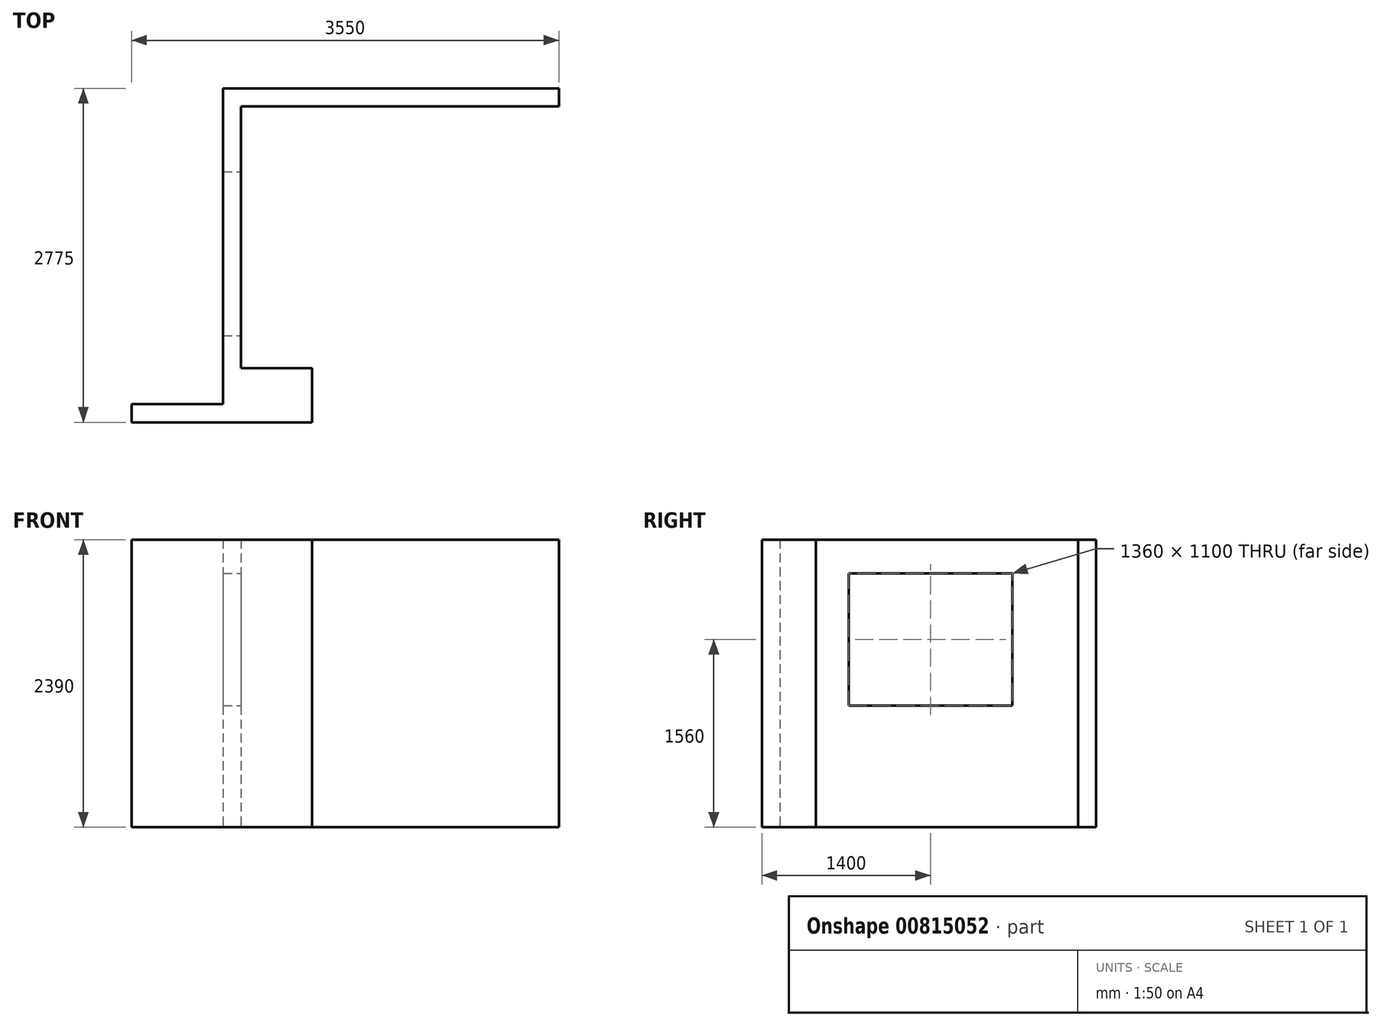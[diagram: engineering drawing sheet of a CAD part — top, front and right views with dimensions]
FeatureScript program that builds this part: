
annotation { "Feature Type Name" : "Feature", "Feature Type Description" : "" }
export const myFeature = defineFeature(function(context is Context, id is Id, definition is map)
    precondition{}
    {
        {
            var Q0;
            Q0=qCreatedBy(makeId("Top.planeOp"),FACE);
            var sketch = newSketch(context, id + "F0", { "sketchPlane" : qUnion([Q0])});
            skLineSegment(sketch, "E0", {"start": v(566.4, 2097.08) * mm, "end": v(566.4, -527.92) * mm});
            skLineSegment(sketch, "E1", {"start": v(566.4, -527.92) * mm, "end": v(716.4, -527.92) * mm});
            skLineSegment(sketch, "E2", {"start": v(716.4, -527.92) * mm, "end": v(716.4, 2247.08) * mm});
            skLineSegment(sketch, "E3", {"start": v(566.4, 2097.08) * mm, "end": v(-2083.6, 2097.08) * mm});
            skLineSegment(sketch, "E4", {"start": v(-2083.6, 2097.08) * mm, "end": v(-2083.6, -77.92) * mm});
            skLineSegment(sketch, "E5", {"start": v(-2083.6, -77.92) * mm, "end": v(-1493.6, -77.92) * mm});
            skLineSegment(sketch, "E6", {"start": v(716.4, 2247.08) * mm, "end": v(-2233.6, 2247.08) * mm});
            skLineSegment(sketch, "E7", {"start": v(-2233.6, 2247.08) * mm, "end": v(-2233.6, -377.92) * mm});
            skLineSegment(sketch, "E8", {"start": v(-2993.6, -527.92) * mm, "end": v(-2993.6, -377.92) * mm});
            skLineSegment(sketch, "E9", {"start": v(-2993.6, -377.92) * mm, "end": v(-2233.6, -377.92) * mm});
            skLineSegment(sketch, "E10", {"start": v(-1493.6, -527.92) * mm, "end": v(-2993.6, -527.92) * mm});
            skLineSegment(sketch, "E11", {"start": v(1616.4, -292.92) * mm, "end": v(2408.2, -292.92) * mm});
            skLineSegment(sketch, "E12", {"start": v(1616.4, 97.08) * mm, "end": v(1616.4, 97.08) * mm});
            skLineSegment(sketch, "E13", {"start": v(1616.4, 1097.08) * mm, "end": v(1616.4, 2097.08) * mm});
            skLineSegment(sketch, "E14", {"start": v(1616.4, 1097.08) * mm, "end": v(1616.4, 1097.08) * mm});
            skLineSegment(sketch, "E15", {"start": v(1616.4, 97.08) * mm, "end": v(2408.2, 97.08) * mm});
            skLineSegment(sketch, "E16", {"start": v(1616.4, -292.92) * mm, "end": v(1616.4, 97.08) * mm});
            skLineSegment(sketch, "E17", {"start": v(1616.4, 1097.08) * mm, "end": v(2417.61, 1097.08) * mm});
            skLineSegment(sketch, "E18", {"start": v(2408.2, -292.92) * mm, "end": v(2408.2, -7632.92) * mm});
            skLineSegment(sketch, "E19", {"start": v(2408.2, -7632.92) * mm, "end": v(-2131.8, -7632.92) * mm});
            skLineSegment(sketch, "E20", {"start": v(-2131.8, -7632.92) * mm, "end": v(-2131.8, -5762.92) * mm});
            skLineSegment(sketch, "E21", {"start": v(-2131.8, -5762.92) * mm, "end": v(-1531.8, -5762.92) * mm});
            skLineSegment(sketch, "E22", {"start": v(-1531.8, -5762.92) * mm, "end": v(-1531.8, -5407.77) * mm});
            skLineSegment(sketch, "E23", {"start": v(-1531.8, -5407.77) * mm, "end": v(-3031.8, -5407.77) * mm});
            skLineSegment(sketch, "E24", {"start": v(-3031.8, -5407.77) * mm, "end": v(-3031.8, -5557.77) * mm});
            skLineSegment(sketch, "E25", {"start": v(2408.2, 97.08) * mm, "end": v(2558.2, 97.08) * mm});
            skLineSegment(sketch, "E26", {"start": v(2558.2, 97.08) * mm, "end": v(2558.2, -7787.07) * mm});
            skLineSegment(sketch, "E27.0", {"start": v(2558.2, -7782.92) * mm, "end": v(-2281.8, -7782.92) * mm});
            skLineSegment(sketch, "E28.0", {"start": v(-2281.8, -7782.92) * mm, "end": v(-2281.8, -5557.77) * mm});
            skLineSegment(sketch, "E29.0", {"start": v(-2281.8, -5557.77) * mm, "end": v(-3031.8, -5557.77) * mm});
            skLineSegment(sketch, "E30", {"start": v(-1493.6, -77.92) * mm, "end": v(-1493.6, -527.92) * mm});
            skSolve(sketch);
        }
        {
            var Q0;
            Q0=makeQuery(id+"F0.imprint","IMPRINT",FACE,{"disambiguationData":[TD([[makeQuery(id+"F0.imprint","IMPRINT",EDGE,{"derivedFrom":sQuery(id+"F0.wireOp",EDGE,"E0")}),1.0]])]});
            var sketch = newSketch(context, id + "F1", { "sketchPlane" : qUnion([Q0])});
            skLineSegment(sketch, "E31", {"start": v(-1610.92, 7669.93) * mm, "end": v(-1610.92, 5044.93) * mm});
            skLineSegment(sketch, "E32", {"start": v(-1610.92, 5044.93) * mm, "end": v(-1460.92, 5044.93) * mm});
            skLineSegment(sketch, "E33", {"start": v(-1460.92, 5044.93) * mm, "end": v(-1460.92, 7819.93) * mm});
            skLineSegment(sketch, "E34", {"start": v(-1610.92, 7669.93) * mm, "end": v(-4260.92, 7669.93) * mm});
            skLineSegment(sketch, "E35", {"start": v(-4260.92, 7669.93) * mm, "end": v(-4260.92, 5494.93) * mm});
            skLineSegment(sketch, "E36", {"start": v(-4260.92, 5494.93) * mm, "end": v(-3670.92, 5494.93) * mm});
            skLineSegment(sketch, "E37", {"start": v(-1460.92, 7819.93) * mm, "end": v(-4410.92, 7819.93) * mm});
            skLineSegment(sketch, "E38", {"start": v(-4410.92, 7819.93) * mm, "end": v(-4410.92, 5194.93) * mm});
            skLineSegment(sketch, "E39", {"start": v(-5170.92, 5044.93) * mm, "end": v(-5170.92, 5194.93) * mm});
            skLineSegment(sketch, "E40", {"start": v(-5170.92, 5194.93) * mm, "end": v(-4410.92, 5194.93) * mm});
            skLineSegment(sketch, "E41", {"start": v(-3670.92, 5044.93) * mm, "end": v(-5170.92, 5044.93) * mm});
            skLineSegment(sketch, "E42", {"start": v(-560.92, 5279.93) * mm, "end": v(230.88, 5279.93) * mm});
            skLineSegment(sketch, "E43", {"start": v(-560.92, 5669.93) * mm, "end": v(-560.92, 5669.93) * mm});
            skLineSegment(sketch, "E44", {"start": v(-560.92, 6669.93) * mm, "end": v(-560.92, 7669.93) * mm});
            skLineSegment(sketch, "E45", {"start": v(-560.92, 6669.93) * mm, "end": v(-560.92, 6669.93) * mm});
            skLineSegment(sketch, "E46", {"start": v(-560.92, 5669.93) * mm, "end": v(230.88, 5669.93) * mm});
            skLineSegment(sketch, "E47", {"start": v(-560.92, 5279.93) * mm, "end": v(-560.92, 5669.93) * mm});
            skLineSegment(sketch, "E48", {"start": v(-560.92, 6669.93) * mm, "end": v(240.28, 6669.93) * mm});
            skLineSegment(sketch, "E49", {"start": v(230.88, 5279.93) * mm, "end": v(230.88, -2060.07) * mm});
            skLineSegment(sketch, "E50", {"start": v(230.88, -2060.07) * mm, "end": v(-4309.12, -2060.07) * mm});
            skLineSegment(sketch, "E51", {"start": v(-4309.12, -2060.07) * mm, "end": v(-4309.12, -190.07) * mm});
            skLineSegment(sketch, "E52", {"start": v(-4309.12, -190.07) * mm, "end": v(-3709.12, -190.07) * mm});
            skLineSegment(sketch, "E53", {"start": v(-3709.12, -190.07) * mm, "end": v(-3709.12, 165.08) * mm});
            skLineSegment(sketch, "E54", {"start": v(-3709.12, 165.08) * mm, "end": v(-5209.12, 165.08) * mm});
            skLineSegment(sketch, "E55", {"start": v(-5209.12, 165.08) * mm, "end": v(-5209.12, 15.08) * mm});
            skLineSegment(sketch, "E56", {"start": v(230.88, 5669.93) * mm, "end": v(380.88, 5669.93) * mm});
            skLineSegment(sketch, "E57", {"start": v(380.88, 5669.93) * mm, "end": v(380.88, -2214.23) * mm});
            skLineSegment(sketch, "E58.0", {"start": v(380.88, -2210.07) * mm, "end": v(-4459.12, -2210.07) * mm});
            skLineSegment(sketch, "E59.0", {"start": v(-4459.12, -2210.07) * mm, "end": v(-4459.12, 15.08) * mm});
            skLineSegment(sketch, "E60.0", {"start": v(-4459.12, 15.08) * mm, "end": v(-5209.12, 15.08) * mm});
            skLineSegment(sketch, "E61", {"start": v(-3670.92, 5494.93) * mm, "end": v(-3670.92, 5044.93) * mm});
            skSolve(sketch);
        }
        {
            var Q0;
            Q0=makeQuery(id+"F1.imprint","IMPRINT",FACE,{"disambiguationData":[TD([[makeQuery(id+"F1.imprint","IMPRINT",EDGE,{"derivedFrom":sQuery(id+"F1.wireOp",EDGE,"E31")}),1.0]])]});
            extrude(context, id + "F2", {"entities" : qUnion([Q0]), "depth" : 2390 * mm, "offsetDistance" : 25 * mm});
        }
        {
            var Q0;
            Q0=makeQuery(id+"F2.opExtrude","SWEPT_FACE",FACE,{"disambiguationData":[OSD([sQuery(id+"F1.wireOp",EDGE,"E35")])]});
            var sketch = newSketch(context, id + "F3", { "sketchPlane" : qUnion([Q0])});
            skLineSegment(sketch, "E62.bottom", {"start": v(5494.93, 2390) * mm, "end": v(5764.93, 2390) * mm, "construction": true});
            skLineSegment(sketch, "E62.top", {"start": v(5494.93, 2110) * mm, "end": v(5764.93, 2110) * mm, "construction": true});
            skLineSegment(sketch, "E62.left", {"start": v(5494.93, 2390) * mm, "end": v(5494.93, 2110) * mm, "construction": true});
            skLineSegment(sketch, "E62.right", {"start": v(5764.93, 2390) * mm, "end": v(5764.93, 2110) * mm, "construction": true});
            skLineSegment(sketch, "E63.bottom", {"start": v(5764.93, 2110) * mm, "end": v(7124.93, 2110) * mm});
            skLineSegment(sketch, "E63.top", {"start": v(5764.93, 1010) * mm, "end": v(7124.93, 1010) * mm});
            skLineSegment(sketch, "E63.left", {"start": v(5764.93, 2110) * mm, "end": v(5764.93, 1010) * mm});
            skLineSegment(sketch, "E63.right", {"start": v(7124.93, 2110) * mm, "end": v(7124.93, 1010) * mm});
            skSolve(sketch);
        }
        {
            var Q0;
            Q0 = qSketchRegion(id + "F3", true);
            var Q1;
            Q1=makeQuery(id+"F2.opExtrude","SWEPT_FACE",FACE,{"disambiguationData":[OSD([sQuery(id+"F1.wireOp",EDGE,"E33")])]});
            extrude(context, id + "F4", {"entities" : qUnion([Q0, Q1]), "operationType" : NewBodyOperationType.REMOVE, "oppositeDirection" : true, "depth" : 160 * mm, "offsetDistance" : 25 * mm});
        }
    });
